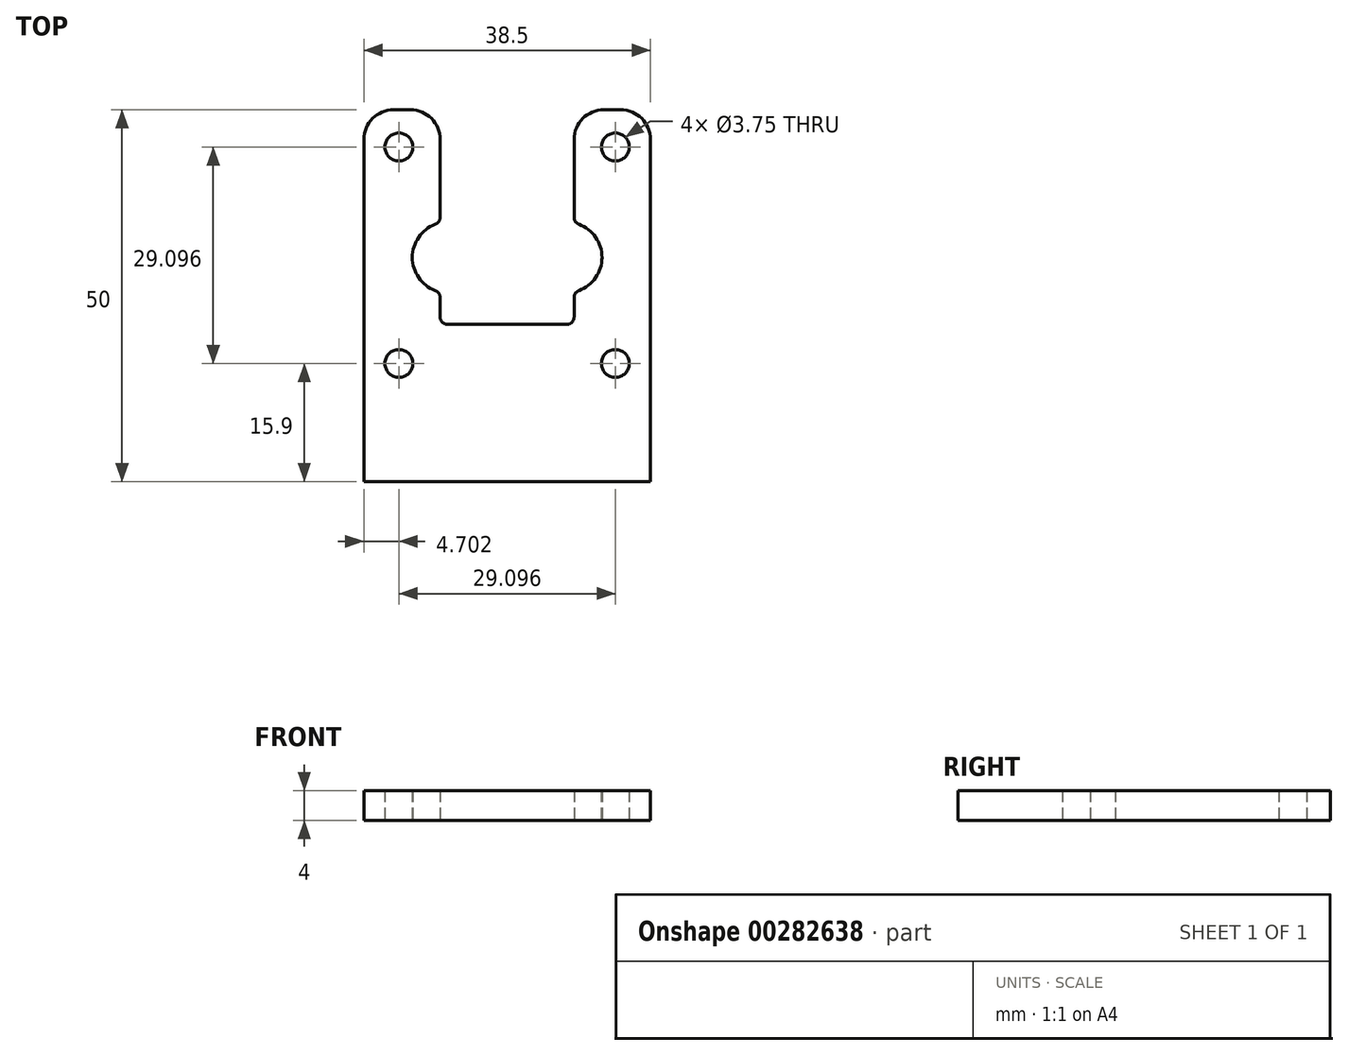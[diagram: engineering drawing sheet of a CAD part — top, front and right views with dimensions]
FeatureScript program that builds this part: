
annotation { "Feature Type Name" : "Feature", "Feature Type Description" : "" }
export const myFeature = defineFeature(function(context is Context, id is Id, definition is map)
    precondition{}
    {
        {
            var Q0;
            Q0=qCreatedBy(makeId("Top.planeOp"),FACE);
            var sketch = newSketch(context, id + "F0", { "sketchPlane" : qUnion([Q0])});
            skLineSegment(sketch, "E0.bottom", {"start": v(19.25, 25.6) * mm, "end": v(9, 25.6) * mm});
            skLineSegment(sketch, "E0.top", {"start": v(19.25, -24.4) * mm, "end": v(-19.25, -24.4) * mm});
            skLineSegment(sketch, "E0.left", {"start": v(19.25, 25.6) * mm, "end": v(19.25, -24.4) * mm});
            skLineSegment(sketch, "E0.right", {"start": v(-19.25, 25.6) * mm, "end": v(-19.25, -24.4) * mm});
            skLineSegment(sketch, "E1.bottom", {"start": v(-9, -3.25) * mm, "end": v(9, -3.25) * mm});
            skLineSegment(sketch, "E1.left", {"start": v(-9, -3.25) * mm, "end": v(-9, 1.1) * mm});
            skLineSegment(sketch, "E1.right", {"start": v(9, -3.25) * mm, "end": v(9, 1.1) * mm});
            skLineSegment(sketch, "E2.trimOffspring", {"start": v(-9, 25.6) * mm, "end": v(-19.25, 25.6) * mm});
            skArc(sketch, "E3", {"start": v(9, 1.1) * mm, "mid": v(12.74, 5.75) * mm, "end": v(9, 10.4) * mm});
            skLineSegment(sketch, "E4.trimOffspring", {"start": v(9, 10.4) * mm, "end": v(9, 25.6) * mm});
            skLineSegment(sketch, "E5", {"start": v(0, -3.25) * mm, "end": v(0, 25.6) * mm, "construction": true});
            skArc(sketch, "E6.MirrorCS", {"start": v(-9, 1.1) * mm, "mid": v(-12.74, 5.75) * mm, "end": v(-9, 10.4) * mm});
            skLineSegment(sketch, "E7.trimOffspring", {"start": v(-9, 10.4) * mm, "end": v(-9, 25.6) * mm});
            skLineSegment(sketch, "E8.bottom", {"start": v(-14.55, -8.5) * mm, "end": v(14.55, -8.5) * mm, "construction": true});
            skLineSegment(sketch, "E8.top", {"start": v(-14.55, 20.6) * mm, "end": v(14.55, 20.6) * mm, "construction": true});
            skLineSegment(sketch, "E8.left", {"start": v(-14.55, -8.5) * mm, "end": v(-14.55, 20.6) * mm, "construction": true});
            skLineSegment(sketch, "E8.right", {"start": v(14.55, -8.5) * mm, "end": v(14.55, 20.6) * mm, "construction": true});
            skLineSegment(sketch, "E9", {"start": v(12.1, 25.6) * mm, "end": v(12.1, 20.6) * mm, "construction": true});
            skLineSegment(sketch, "E10", {"start": v(14.55, 1.56) * mm, "end": v(19.25, 1.56) * mm, "construction": true});
            skLineSegment(sketch, "E11", {"start": v(-14.55, -4.45) * mm, "end": v(-19.25, -4.45) * mm, "construction": true});
            skCircle(sketch, "E12", {"center": v(-14.55, 20.6) * mm, "radius": 1.88 * mm});
            skCircle(sketch, "E13", {"center": v(14.55, 20.6) * mm, "radius": 1.88 * mm});
            skCircle(sketch, "E14", {"center": v(-14.55, -8.5) * mm, "radius": 1.88 * mm});
            skCircle(sketch, "E15", {"center": v(14.55, -8.5) * mm, "radius": 1.88 * mm});
            skSolve(sketch);
        }
        {
            var Q0;
            Q0 = qSketchRegion(id + "F0", true);
            extrude(context, id + "F1", {"entities" : qUnion([Q0]), "depth" : 4 * mm});
        }
        {
            var Q0;
            Q0=makeQuery(id+"F1.opExtrude","SWEPT_EDGE",EDGE,{"disambiguationData":[OSD([sQuery(id+"F0.wireOp",EDGE,"E0.bottom"),sQuery(id+"F0.wireOp",EDGE,"E0.left")])]});
            var Q1;
            Q1=makeQuery(id+"F1.opExtrude","SWEPT_EDGE",EDGE,{"disambiguationData":[OSD([sQuery(id+"F0.wireOp",EDGE,"E0.right"),sQuery(id+"F0.wireOp",EDGE,"E2.trimOffspring")])]});
            var Q2;
            Q2=makeQuery(id+"F1.opExtrude","SWEPT_EDGE",EDGE,{"disambiguationData":[OSD([sQuery(id+"F0.wireOp",EDGE,"E2.trimOffspring"),sQuery(id+"F0.wireOp",EDGE,"E7.trimOffspring")])]});
            var Q3;
            Q3=makeQuery(id+"F1.opExtrude","SWEPT_EDGE",EDGE,{"disambiguationData":[OSD([sQuery(id+"F0.wireOp",EDGE,"E0.bottom"),sQuery(id+"F0.wireOp",EDGE,"E4.trimOffspring")])]});
            fillet(context, id + "F2", {"entities" : qUnion([Q0, Q1, Q2, Q3]), "radius" : 4 * mm, "tangentPropagation" : true, "allowEdgeOverflow" : false});
        }
        {
            var Q0;
            Q0=makeQuery(id+"F1.opExtrude","SWEPT_EDGE",EDGE,{"disambiguationData":[OSD([sQuery(id+"F0.wireOp",EDGE,"E6.MirrorCS"),sQuery(id+"F0.wireOp",EDGE,"E7.trimOffspring")])]});
            var Q1;
            Q1=makeQuery(id+"F1.opExtrude","SWEPT_EDGE",EDGE,{"disambiguationData":[OSD([sQuery(id+"F0.wireOp",EDGE,"E1.left"),sQuery(id+"F0.wireOp",EDGE,"E6.MirrorCS")])]});
            var Q2;
            Q2=makeQuery(id+"F1.opExtrude","SWEPT_EDGE",EDGE,{"disambiguationData":[OSD([sQuery(id+"F0.wireOp",EDGE,"E1.bottom"),sQuery(id+"F0.wireOp",EDGE,"E1.left")])]});
            var Q3;
            Q3=makeQuery(id+"F1.opExtrude","SWEPT_EDGE",EDGE,{"disambiguationData":[OSD([sQuery(id+"F0.wireOp",EDGE,"E1.bottom"),sQuery(id+"F0.wireOp",EDGE,"E1.right")])]});
            var Q4;
            Q4=makeQuery(id+"F1.opExtrude","SWEPT_EDGE",EDGE,{"disambiguationData":[OSD([sQuery(id+"F0.wireOp",EDGE,"E1.right"),sQuery(id+"F0.wireOp",EDGE,"E3")])]});
            var Q5;
            Q5=makeQuery(id+"F1.opExtrude","SWEPT_EDGE",EDGE,{"disambiguationData":[OSD([sQuery(id+"F0.wireOp",EDGE,"E3"),sQuery(id+"F0.wireOp",EDGE,"E4.trimOffspring")])]});
            fillet(context, id + "F3", {"entities" : qUnion([Q0, Q1, Q2, Q3, Q4, Q5]), "radius" : 1 * mm, "tangentPropagation" : true, "allowEdgeOverflow" : false});
        }
    });
